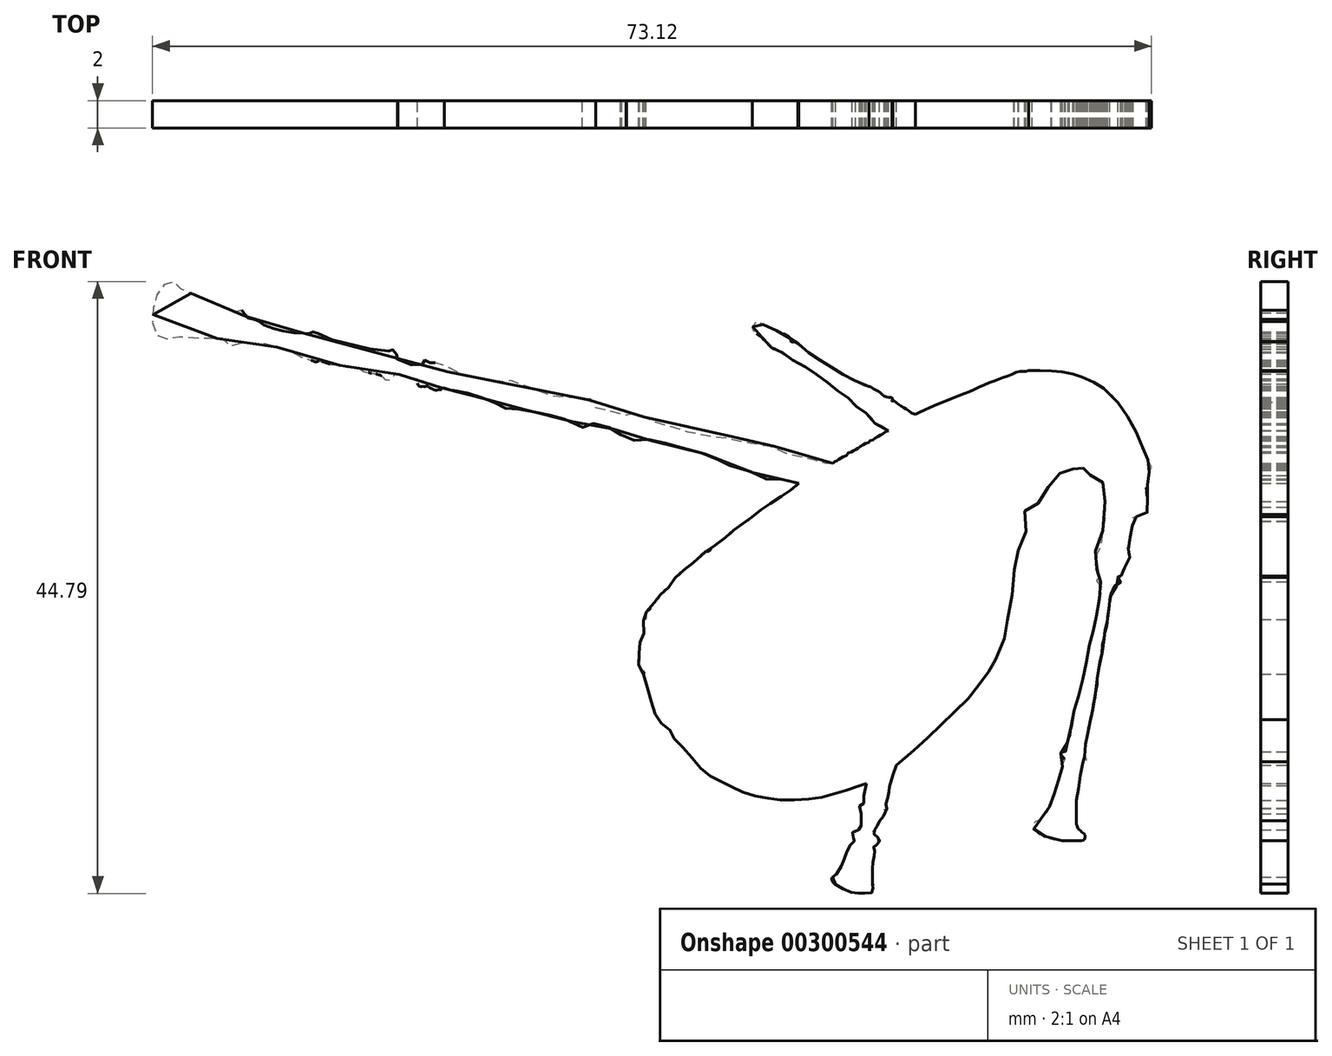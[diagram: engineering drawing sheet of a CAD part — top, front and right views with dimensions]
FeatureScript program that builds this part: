
annotation { "Feature Type Name" : "Feature", "Feature Type Description" : "" }
export const myFeature = defineFeature(function(context is Context, id is Id, definition is map)
    precondition{}
    {
        {
            var Q0;
            Q0=qCreatedBy(makeId("Front.planeOp"),FACE);
            var sketch = newSketch(context, id + "F0", { "sketchPlane" : qUnion([Q0])});
            skFitSpline(sketch, "E0", {"points": [v(-4.4, -4) * mm, v(-4.03, -5.37) * mm, v(-3.62, -6.74) * mm, v(-3.21, -7.5) * mm, v(-2.5, -8.07) * mm, v(-2.19, -8.69) * mm, v(-1.47, -9.44) * mm, v(-0.58, -10.5) * mm, v(0.27, -11.32) * mm, v(1.13, -11.8) * mm, v(1.98, -12.2) * mm, v(3.14, -12.75) * mm, v(4.3, -13) * mm, v(5.4, -13.2) * mm, v(6.8, -13.2) * mm, v(8.2, -13.1) * mm, v(9.33, -12.82) * mm, v(10.45, -12.5) * mm, v(11.54, -12.12) * mm, v(11.9, -12) * mm], "startDerivative": vector(6.1, -22.37) * mm, "endDerivative": vector(9.97, 3.21) * mm});
            skFitSpline(sketch, "E1", {"points": [v(11.9, -12) * mm, v(11.73, -12.78) * mm, v(11.66, -13.2) * mm, v(11.63, -13.38) * mm, v(11.78, -13.52) * mm, v(11.43, -13.58) * mm, v(11.44, -13.79) * mm, v(11.52, -13.94) * mm, v(11.5, -14.57) * mm, v(11.52, -15.1) * mm, v(11.5, -15.34) * mm, v(11.38, -15.4) * mm, v(11.26, -15.39) * mm, v(10.97, -15.48) * mm, v(10.88, -15.6) * mm, v(10.85, -15.8) * mm, v(10.88, -15.93) * mm, v(10.97, -15.98) * mm, v(11.04, -16.07) * mm, v(11.1, -16.14) * mm, v(11.03, -16.21) * mm, v(10.88, -16.25) * mm, v(10.77, -16.42) * mm, v(10.69, -16.6) * mm, v(10.56, -16.86) * mm, v(10.45, -17.04) * mm, v(10.34, -17.33) * mm, v(10.24, -17.6) * mm, v(10.13, -17.9) * mm, v(10, -18.16) * mm, v(9.82, -18.53) * mm, v(9.64, -18.75) * mm, v(9.65, -18.85) * mm, v(9.4, -18.86) * mm, v(9.46, -19.23) * mm, v(9.72, -19.44) * mm, v(10.06, -19.64) * mm, v(10.31, -19.75) * mm, v(10.67, -19.93) * mm, v(11, -20.02) * mm, v(11.16, -20.02) * mm, v(11.35, -20.03) * mm, v(11.6, -20.04) * mm, v(11.8, -20.04) * mm, v(12.04, -20.05) * mm, v(12.25, -20) * mm, v(12.4, -19.91) * mm, v(12.44, -19.78) * mm, v(12.37, -19.69) * mm, v(12.37, -19.65) * mm, v(12.38, -19.5) * mm, v(12.36, -19.37) * mm, v(12.34, -19.35) * mm], "startDerivative": vector(-5.6, -22.68) * mm, "endDerivative": vector(-3.27, 1.97) * mm});
            skFitSpline(sketch, "E2", {"points": [v(12.34, -19.35) * mm, v(12.34, -19.23) * mm, v(12.35, -19.04) * mm, v(12.34, -18.88) * mm, v(12.34, -18.73) * mm, v(12.34, -18.54) * mm, v(12.34, -18.4) * mm, v(12.34, -18.26) * mm, v(12.34, -18.1) * mm, v(12.34, -17.94) * mm, v(12.4, -17.62) * mm, v(12.44, -17.4) * mm, v(12.52, -17.17) * mm, v(12.52, -17.09) * mm, v(12.52, -16.96) * mm, v(12.5, -16.84) * mm, v(12.44, -16.8) * mm, v(12.44, -16.68) * mm, v(12.4, -16.56) * mm, v(12.53, -16.51) * mm, v(12.65, -16.5) * mm, v(12.76, -16.43) * mm, v(12.81, -16.33) * mm, v(12.85, -16.2) * mm, v(12.84, -16.08) * mm, v(12.76, -15.97) * mm, v(12.65, -15.9) * mm, v(12.5, -15.77) * mm, v(12.44, -15.67) * mm, v(12.44, -15.53) * mm, v(12.49, -15.42) * mm, v(12.54, -15.32) * mm, v(12.61, -15.2) * mm, v(12.7, -15.1) * mm, v(12.75, -15.03) * mm, v(12.83, -14.81) * mm, v(12.93, -14.64) * mm, v(13.1, -14.46) * mm, v(13.2, -14.33) * mm, v(13.3, -14.21) * mm, v(13.26, -13.95) * mm, v(13.23, -13.8) * mm, v(13.41, -13.83) * mm, v(13.3, -13.63) * mm, v(13.3, -13.52) * mm, v(13.37, -13.32) * mm, v(13.44, -13.13) * mm, v(13.5, -12.8) * mm, v(13.54, -12.65) * mm, v(13.57, -12.48) * mm, v(13.58, -12.34) * mm, v(13.6, -12.15) * mm, v(13.92, -11.21) * mm, v(14.09, -10.66) * mm], "startDerivative": vector(-0.15, 7.17) * mm, "endDerivative": vector(4.14, 13.76) * mm});
            skFitSpline(sketch, "E3", {"points": [v(14.09, -10.66) * mm, v(14.34, -10.47) * mm, v(14.73, -10.14) * mm, v(15.12, -9.8) * mm, v(15.34, -9.6) * mm, v(15.6, -9.39) * mm, v(15.81, -9.2) * mm, v(16.03, -9) * mm, v(16.28, -8.77) * mm, v(16.46, -8.6) * mm, v(16.66, -8.46) * mm, v(16.9, -8.22) * mm, v(17.09, -8.01) * mm, v(17.3, -7.82) * mm, v(17.47, -7.6) * mm, v(17.74, -7.44) * mm, v(17.93, -7.24) * mm, v(18.1, -7.05) * mm, v(18.3, -6.8) * mm, v(18.52, -6.66) * mm, v(18.7, -6.43) * mm, v(19, -6.18) * mm, v(19.2, -5.92) * mm, v(19.35, -5.77) * mm, v(19.6, -5.58) * mm, v(19.69, -5.43) * mm, v(19.85, -5.23) * mm, v(20.02, -4.98) * mm, v(20.12, -4.8) * mm, v(20.27, -4.56) * mm, v(20.43, -4.44) * mm, v(20.54, -4.24) * mm, v(20.63, -4.08) * mm, v(20.8, -3.88) * mm, v(20.88, -3.71) * mm, v(20.95, -3.58) * mm, v(21.02, -3.48) * mm, v(21.15, -3.33) * mm, v(21.22, -3.17) * mm, v(21.29, -3.06) * mm, v(21.36, -2.93) * mm, v(21.42, -2.78) * mm, v(21.73, -2.09) * mm, v(21.9, -1.7) * mm, v(21.98, -1.45) * mm, v(22.06, -1.14) * mm, v(22.12, -0.89) * mm, v(22.15, -0.65) * mm, v(22.19, -0.35) * mm, v(22.2, -0.12) * mm, v(22.28, 0.29) * mm, v(22.33, 0.67) * mm, v(22.53, 1.49) * mm, v(22.58, 1.94) * mm, v(22.69, 2.7) * mm, v(22.69, 3.04) * mm, v(22.73, 3.47) * mm, v(22.7, 3.96) * mm, v(22.71, 4.37) * mm, v(22.87, 4.56) * mm, v(23.03, 4.74) * mm, v(23, 5.17) * mm, v(23.15, 5.44) * mm, v(23.33, 5.75) * mm, v(23.51, 6.09) * mm, v(23.58, 6.46) * mm, v(23.6, 6.85) * mm, v(23.58, 7.1) * mm, v(23.55, 7.45) * mm, v(23.52, 7.66) * mm, v(23.54, 8.1) * mm, v(23.72, 8.18) * mm, v(23.96, 8.22) * mm, v(24.14, 8.23) * mm, v(24.36, 8.4) * mm, v(24.5, 8.55) * mm, v(24.63, 8.78) * mm, v(24.73, 8.9) * mm, v(24.86, 9.16) * mm, v(25.04, 9.45) * mm, v(25.28, 9.78) * mm, v(25.54, 10.22) * mm, v(25.73, 10.4) * mm, v(25.86, 10.5) * mm, v(25.98, 10.66) * mm, v(26.05, 10.71) * mm, v(26.16, 10.88) * mm, v(26.3, 11) * mm, v(26.54, 10.96) * mm, v(26.66, 10.92) * mm, v(26.88, 10.96) * mm, v(27.05, 11.03) * mm, v(27.22, 11.14) * mm, v(27.34, 11.28) * mm, v(27.46, 11.34) * mm, v(27.6, 11.25) * mm, v(27.68, 11.17) * mm, v(27.71, 11.1) * mm, v(27.84, 11.07) * mm, v(27.99, 11.06) * mm, v(28.16, 11.06) * mm, v(28.27, 11.04) * mm, v(28.28, 10.9) * mm, v(28.27, 10.77) * mm, v(28.26, 10.65) * mm, v(28.3, 10.54) * mm, v(28.4, 10.42) * mm, v(28.55, 10.33) * mm, v(28.74, 10.22) * mm, v(28.88, 10.23) * mm, v(29.13, 10.16) * mm, v(29.2, 9.9) * mm, v(29.11, 9.54) * mm, v(29.1, 9.24) * mm, v(29.23, 8.92) * mm, v(29.37, 8.63) * mm], "startDerivative": vector(24.42, 19.4) * mm, "endDerivative": vector(13.5, -29.6) * mm});
            skFitSpline(sketch, "E4", {"points": [v(29.37, 8.63) * mm, v(29.37, 8.2) * mm, v(29.37, 7.91) * mm, v(29.37, 7.56) * mm, v(29.26, 7.1) * mm, v(29.22, 6.78) * mm, v(29.18, 6.27) * mm, v(29.08, 5.97) * mm, v(29.05, 5.62) * mm, v(29.05, 5.36) * mm, v(28.95, 5.28) * mm, v(28.82, 5.2) * mm, v(28.67, 5.1) * mm, v(28.69, 4.9) * mm, v(28.77, 4.7) * mm, v(28.82, 4.64) * mm, v(28.73, 4.48) * mm, v(28.67, 4.37) * mm, v(28.77, 4.31) * mm, v(28.78, 4.1) * mm, v(28.74, 3.85) * mm, v(28.75, 3.65) * mm, v(28.77, 3.47) * mm, v(28.93, 3.33) * mm, v(28.73, 3.29) * mm, v(28.65, 3.13) * mm, v(28.69, 2.94) * mm, v(28.77, 2.82) * mm, v(28.93, 2.77) * mm, v(29.07, 2.76) * mm, v(29.12, 2.63) * mm, v(29.12, 2.51) * mm, v(29.1, 2.3) * mm, v(29.08, 2.14) * mm, v(29.08, 1.97) * mm, v(29.02, 1.75) * mm, v(29.02, 1.68) * mm, v(29, 1.6) * mm, v(28.96, 1.48) * mm, v(28.91, 1.37) * mm, v(28.92, 1.19) * mm, v(28.9, 1.1) * mm, v(28.86, 0.96) * mm, v(28.83, 0.73) * mm, v(28.8, 0.6) * mm, v(28.78, 0.48) * mm, v(28.76, 0.34) * mm, v(28.73, 0.22) * mm, v(28.71, 0.11) * mm, v(28.69, 0) * mm, v(28.67, -0.08) * mm, v(28.66, -0.16) * mm, v(28.66, -0.26) * mm, v(28.62, -0.42) * mm, v(28.62, -0.48) * mm, v(28.58, -0.56) * mm, v(28.56, -0.64) * mm, v(28.53, -0.75) * mm, v(28.52, -0.82) * mm, v(28.5, -0.9) * mm, v(28.5, -0.95) * mm, v(28.46, -1.03) * mm, v(28.42, -1.15) * mm, v(28.42, -1.2) * mm, v(28.37, -1.3) * mm, v(28.35, -1.41) * mm, v(28.33, -1.53) * mm, v(28.32, -1.59) * mm, v(28.3, -1.67) * mm, v(28.24, -1.82) * mm, v(28.2, -2.09) * mm, v(28.16, -2.31) * mm, v(28.13, -2.5) * mm, v(28.1, -2.64) * mm, v(28.05, -2.82) * mm, v(28.04, -2.87) * mm, v(28.02, -2.93) * mm, v(28.02, -3) * mm, v(28.01, -3.06) * mm, v(28, -3.14) * mm, v(27.99, -3.21) * mm, v(27.97, -3.33) * mm, v(27.96, -3.4) * mm, v(27.95, -3.45) * mm, v(27.92, -3.55) * mm, v(27.88, -3.64) * mm, v(27.86, -3.85) * mm, v(27.8, -4.05) * mm, v(27.78, -4.24) * mm, v(27.73, -4.38) * mm, v(27.67, -4.54) * mm, v(27.6, -4.72) * mm, v(27.55, -4.93) * mm, v(27.5, -5.08) * mm, v(27.5, -5.2) * mm, v(27.48, -5.3) * mm, v(27.47, -5.43) * mm, v(27.44, -5.53) * mm, v(27.42, -5.65) * mm, v(27.39, -5.75) * mm, v(27.37, -5.83) * mm, v(27.34, -5.94) * mm, v(27.32, -6.03) * mm, v(27.3, -6.13) * mm, v(27.29, -6.2) * mm, v(27.25, -6.26) * mm, v(27.24, -6.34) * mm, v(27.2, -6.43) * mm, v(27.16, -6.54) * mm, v(27.11, -6.63) * mm, v(27.1, -6.78) * mm, v(27.05, -7) * mm, v(27, -7.19) * mm, v(27, -7.33) * mm, v(26.95, -7.56) * mm, v(26.94, -7.64) * mm, v(26.9, -7.75) * mm, v(26.87, -7.9) * mm, v(26.84, -8.02) * mm, v(26.82, -8.16) * mm, v(26.8, -8.35) * mm, v(26.78, -8.47) * mm, v(26.77, -8.57) * mm, v(26.76, -8.63) * mm, v(26.7, -8.67) * mm, v(26.68, -8.78) * mm, v(26.67, -8.86) * mm, v(26.64, -8.93) * mm, v(26.62, -9.04) * mm, v(26.6, -9.13) * mm, v(26.57, -9.22) * mm, v(26.56, -9.3) * mm, v(26.53, -9.4) * mm, v(26.52, -9.48) * mm, v(26.48, -9.6) * mm, v(26.47, -9.67) * mm, v(26.33, -9.68) * mm, v(26.26, -9.68) * mm, v(26.23, -9.7) * mm, v(26.16, -9.76) * mm, v(26.13, -9.87) * mm, v(26.16, -9.9) * mm, v(26.2, -9.97) * mm, v(26.27, -10.03) * mm, v(26.29, -10.06) * mm, v(26.35, -10.12) * mm, v(26.4, -10.18) * mm, v(26.36, -10.37) * mm, v(26.33, -10.49) * mm, v(26.27, -10.6) * mm, v(26.25, -10.66) * mm, v(26.25, -10.76) * mm, v(26.21, -10.82) * mm, v(26.2, -10.95) * mm, v(26.16, -11.06) * mm, v(26.14, -11.16) * mm, v(26.12, -11.21) * mm, v(26.12, -11.28) * mm, v(26.1, -11.35) * mm, v(26.05, -11.48) * mm, v(26.04, -11.56) * mm, v(26, -11.65) * mm, v(25.97, -11.73) * mm, v(25.91, -11.83) * mm, v(25.9, -11.94) * mm, v(25.88, -12) * mm, v(25.86, -12.15) * mm, v(25.83, -12.15) * mm, v(25.8, -12.24) * mm, v(25.76, -12.34) * mm, v(25.75, -12.48) * mm, v(25.74, -12.56) * mm, v(25.68, -12.65) * mm, v(25.65, -12.73) * mm, v(25.63, -12.8) * mm, v(25.6, -12.95) * mm, v(25.59, -13) * mm, v(25.53, -13.07) * mm, v(25.5, -13.1) * mm, v(25.47, -13.18) * mm, v(25.44, -13.28) * mm, v(25.45, -13.36) * mm, v(25.4, -13.44) * mm, v(25.38, -13.48) * mm, v(25.34, -13.62) * mm, v(25.31, -13.7) * mm, v(25.26, -13.84) * mm, v(25.18, -14) * mm, v(25.13, -14.12) * mm, v(25.07, -14.21) * mm, v(25.03, -14.21) * mm, v(24.97, -14.32) * mm, v(24.9, -14.38) * mm, v(24.85, -14.43) * mm, v(24.8, -14.48) * mm, v(24.74, -14.52) * mm, v(24.6, -14.65) * mm, v(24.55, -14.7) * mm, v(24.4, -14.76) * mm, v(24.34, -14.77) * mm, v(24.27, -14.79) * mm, v(24.1, -14.8) * mm, v(24.07, -14.9) * mm, v(24.04, -15.05) * mm, v(24.08, -15.18) * mm, v(24.11, -15.3) * mm, v(24.16, -15.35) * mm, v(24.2, -15.42) * mm, v(24.27, -15.47) * mm, v(24.33, -15.51) * mm, v(24.42, -15.58) * mm, v(24.45, -15.61) * mm, v(24.5, -15.66) * mm, v(24.6, -15.7) * mm, v(24.63, -15.75) * mm, v(24.7, -15.78) * mm, v(24.78, -15.83) * mm, v(24.93, -15.86) * mm, v(25, -15.88) * mm, v(25.1, -15.94) * mm, v(25.21, -16) * mm, v(25.33, -16.02) * mm, v(25.46, -16.07) * mm, v(25.58, -16.1) * mm, v(25.67, -16.13) * mm, v(25.73, -16.13) * mm, v(25.92, -16.14) * mm, v(26.2, -16.19) * mm], "startDerivative": vector(0.28, -53.15) * mm, "endDerivative": vector(42.65, -6.9) * mm});
            skFitSpline(sketch, "E5", {"points": [v(26.2, -16.19) * mm, v(26.4, -16.19) * mm, v(26.56, -16.19) * mm, v(26.83, -16.19) * mm, v(26.97, -16.19) * mm, v(27.24, -16.19) * mm, v(27.3, -16.19) * mm, v(27.54, -16.19) * mm, v(27.7, -16.19) * mm, v(27.84, -16.1) * mm, v(27.9, -16.02) * mm, v(27.9, -15.87) * mm, v(27.88, -15.76) * mm, v(27.84, -15.7) * mm, v(27.8, -15.65) * mm, v(27.72, -15.6) * mm, v(27.66, -15.54) * mm, v(27.6, -15.48) * mm, v(27.55, -15.43) * mm, v(27.5, -15.4) * mm, v(27.46, -15.37) * mm, v(27.4, -15.3) * mm, v(27.37, -15.3) * mm, v(27.34, -15.18) * mm, v(27.3, -15.03) * mm, v(27.27, -14.93) * mm, v(27.27, -14.8) * mm, v(27.28, -14.71) * mm], "startDerivative": vector(4.3, 0) * mm, "endDerivative": vector(0.55, 2.5) * mm});
            skFitSpline(sketch, "E6", {"points": [v(27.28, -14.71) * mm, v(27.27, -14.63) * mm, v(27.27, -14.56) * mm, v(27.27, -14.5) * mm, v(27.27, -14.43) * mm, v(27.27, -14.36) * mm, v(27.27, -14.3) * mm, v(27.27, -14.23) * mm, v(27.27, -14.17) * mm, v(27.28, -14.13) * mm, v(27.28, -14.04) * mm, v(27.28, -13.99) * mm, v(27.28, -13.92) * mm, v(27.28, -13.9) * mm, v(27.28, -13.83) * mm, v(27.28, -13.77) * mm, v(27.28, -13.7) * mm, v(27.3, -13.66) * mm, v(27.3, -13.62) * mm, v(27.3, -13.58) * mm, v(27.3, -13.56) * mm, v(27.3, -13.48) * mm, v(27.3, -13.46) * mm, v(27.28, -13.35) * mm, v(27.28, -13.24) * mm, v(27.28, -13.14) * mm, v(27.28, -13.06) * mm, v(27.28, -13) * mm, v(27.4, -12.93) * mm, v(27.4, -12.83) * mm, v(27.4, -12.63) * mm, v(27.4, -12.57) * mm, v(27.4, -12.5) * mm, v(27.4, -12.43) * mm, v(27.46, -12.35) * mm, v(27.46, -12.22) * mm, v(27.46, -12.15) * mm, v(27.47, -12.04) * mm, v(27.47, -11.94) * mm, v(27.47, -11.8) * mm, v(27.47, -11.65) * mm, v(27.54, -11.56) * mm, v(27.54, -11.48) * mm, v(27.54, -11.38) * mm, v(27.54, -11.3) * mm, v(27.54, -11.18) * mm, v(27.54, -11.09) * mm, v(27.7, -10.95) * mm, v(27.7, -10.7) * mm, v(27.7, -10.62) * mm, v(27.7, -10.54) * mm, v(27.75, -10.5) * mm, v(27.8, -10.42) * mm, v(27.84, -10.42) * mm, v(27.91, -10.4) * mm, v(27.93, -10.4) * mm, v(27.96, -10.37) * mm, v(27.98, -10.34) * mm, v(28.01, -10.31) * mm, v(28.02, -10.27) * mm, v(28.02, -10.24) * mm, v(28.02, -10.18) * mm, v(28, -10.14) * mm, v(27.98, -10.1) * mm, v(27.9, -10.05) * mm, v(27.85, -10) * mm, v(27.87, -9.96) * mm, v(27.87, -9.85) * mm, v(27.86, -9.81) * mm, v(27.87, -9.67) * mm, v(27.86, -9.56) * mm, v(27.88, -9.48) * mm, v(27.93, -9.35) * mm, v(27.93, -9.23) * mm, v(27.94, -9.17) * mm, v(27.95, -9.12) * mm, v(27.97, -9.01) * mm, v(28, -8.94) * mm, v(28.03, -8.8) * mm, v(28.03, -8.78) * mm, v(28.05, -8.67) * mm, v(28.04, -8.63) * mm, v(28.05, -8.59) * mm, v(28.07, -8.52) * mm, v(28.08, -8.45) * mm, v(28.09, -8.42) * mm, v(28.1, -8.35) * mm, v(28.1, -8.32) * mm, v(28.1, -8.28) * mm, v(28.1, -8.2) * mm, v(28.1, -8.16) * mm, v(28.12, -8.1) * mm, v(28.14, -8.06) * mm, v(28.15, -8) * mm, v(28.15, -7.95) * mm, v(28.16, -7.93) * mm, v(28.18, -7.88) * mm, v(28.2, -7.83) * mm, v(28.22, -7.77) * mm, v(28.23, -7.73) * mm, v(28.24, -7.7) * mm, v(28.25, -7.65) * mm, v(28.26, -7.59) * mm, v(28.26, -7.54) * mm, v(28.27, -7.47) * mm, v(28.27, -7.46) * mm, v(28.27, -7.45) * mm, v(28.3, -7.37) * mm, v(28.3, -7.37) * mm, v(28.3, -7.33) * mm, v(28.3, -7.33) * mm, v(28.31, -7.28) * mm, v(28.32, -7.21) * mm, v(28.34, -7.18) * mm, v(28.36, -7.13) * mm, v(28.37, -7.1) * mm, v(28.37, -7.08) * mm, v(28.38, -7.05) * mm, v(28.38, -7.04) * mm, v(28.38, -7) * mm, v(28.39, -6.95) * mm, v(28.39, -6.92) * mm, v(28.39, -6.9) * mm, v(28.4, -6.87) * mm, v(28.42, -6.81) * mm, v(28.43, -6.78) * mm, v(28.43, -6.74) * mm, v(28.44, -6.7) * mm, v(28.44, -6.67) * mm, v(28.45, -6.65) * mm, v(28.45, -6.63) * mm, v(28.47, -6.58) * mm, v(28.47, -6.56) * mm, v(28.48, -6.52) * mm, v(28.48, -6.5) * mm, v(28.49, -6.47) * mm, v(28.49, -6.45) * mm, v(28.49, -6.41) * mm, v(28.5, -6.38) * mm, v(28.49, -6.36) * mm, v(28.5, -6.34) * mm, v(28.5, -6.32) * mm, v(28.5, -6.3) * mm, v(28.5, -6.28) * mm, v(28.51, -6.21) * mm, v(28.53, -6.1) * mm, v(28.57, -6) * mm, v(28.61, -5.9) * mm, v(28.64, -5.76) * mm, v(28.63, -5.64) * mm, v(28.62, -5.57) * mm, v(28.62, -5.52) * mm, v(28.65, -5.43) * mm, v(28.66, -5.35) * mm, v(28.67, -5.3) * mm, v(28.68, -5.23) * mm, v(28.7, -5.17) * mm, v(28.72, -5.09) * mm, v(28.73, -5.02) * mm, v(28.76, -4.95) * mm, v(28.77, -4.86) * mm, v(28.79, -4.75) * mm, v(28.79, -4.74) * mm, v(28.8, -4.7) * mm, v(28.8, -4.62) * mm, v(28.8, -4.53) * mm, v(28.79, -4.5) * mm, v(28.79, -4.42) * mm, v(28.79, -4.34) * mm, v(28.8, -4.28) * mm, v(28.8, -4.25) * mm, v(28.8, -4.19) * mm, v(28.8, -4.15) * mm, v(28.84, -3.96) * mm, v(28.84, -3.81) * mm, v(28.9, -3.61) * mm, v(28.91, -3.54) * mm, v(28.95, -3.42) * mm, v(28.96, -3.29) * mm, v(28.96, -3.17) * mm, v(29, -3.03) * mm, v(29.06, -2.89) * mm, v(29.12, -2.76) * mm, v(29.15, -2.62) * mm, v(29.15, -2.5) * mm, v(29.17, -2.37) * mm, v(29.17, -2.27) * mm, v(29.18, -2.1) * mm, v(29.2, -2) * mm, v(29.18, -1.83) * mm, v(29.18, -1.8) * mm, v(29.26, -1.63) * mm, v(29.26, -1.59) * mm, v(29.26, -1.52) * mm, v(29.28, -1.47) * mm, v(29.29, -1.44) * mm, v(29.3, -1.4) * mm, v(29.3, -1.36) * mm, v(29.32, -1.3) * mm, v(29.32, -1.24) * mm, v(29.33, -1.2) * mm, v(29.33, -1.15) * mm, v(29.33, -1.13) * mm, v(29.33, -1.12) * mm, v(29.33, -1.05) * mm, v(29.32, -0.98) * mm, v(29.34, -0.9) * mm, v(29.37, -0.87) * mm, v(29.37, -0.85) * mm, v(29.37, -0.8) * mm, v(29.41, -0.73) * mm, v(29.43, -0.68) * mm, v(29.45, -0.58) * mm, v(29.44, -0.52) * mm, v(29.46, -0.46) * mm, v(29.46, -0.45) * mm, v(29.46, -0.42) * mm, v(29.47, -0.38) * mm, v(29.49, -0.34) * mm, v(29.5, -0.3) * mm, v(29.53, -0.26) * mm, v(29.53, -0.2) * mm, v(29.53, -0.18) * mm, v(29.54, -0.13) * mm, v(29.56, -0.09) * mm, v(29.56, -0.03) * mm, v(29.56, 0) * mm, v(29.56, 0.11) * mm, v(29.54, 0.2) * mm, v(29.53, 0.28) * mm, v(29.56, 0.46) * mm, v(29.6, 0.6) * mm, v(29.63, 0.72) * mm, v(29.67, 0.9) * mm, v(29.67, 0.94) * mm, v(29.68, 1.01) * mm, v(29.7, 1.1) * mm, v(29.7, 1.2) * mm, v(29.7, 1.3) * mm, v(29.7, 1.42) * mm, v(29.71, 1.53) * mm, v(29.73, 1.61) * mm, v(29.76, 1.68) * mm, v(29.78, 1.8) * mm, v(29.82, 1.9) * mm, v(29.85, 1.97) * mm, v(29.88, 2.09) * mm, v(29.92, 2.22) * mm, v(29.97, 2.33) * mm, v(30.08, 2.46) * mm, v(30.17, 2.48) * mm, v(30.29, 2.5) * mm, v(30.33, 2.5) * mm, v(30.43, 2.6) * mm, v(30.49, 2.7) * mm, v(30.5, 2.77) * mm, v(30.5, 2.82) * mm, v(30.5, 2.9) * mm, v(30.48, 2.93) * mm, v(30.47, 2.96) * mm, v(30.4, 3.02) * mm, v(30.33, 3.08) * mm, v(30.33, 3.08) * mm], "startDerivative": vector(-1.8, 19.18) * mm, "endDerivative": vector(-3.69, -1.3) * mm});
            skFitSpline(sketch, "E7", {"points": [v(30.33, 3.08) * mm, v(30.33, 3.14) * mm, v(30.4, 3.15) * mm, v(30.46, 3.17) * mm, v(30.52, 3.18) * mm, v(30.52, 3.18) * mm], "startDerivative": vector(-0.05, 0.33) * mm, "endDerivative": vector(0.07, 0) * mm});
            skFitSpline(sketch, "E8", {"points": [v(30.52, 3.18) * mm, v(30.58, 3.18) * mm, v(30.61, 3.2) * mm, v(30.65, 3.23) * mm, v(30.66, 3.3) * mm, v(30.66, 3.35) * mm, v(30.65, 3.4) * mm, v(30.66, 3.5) * mm, v(30.67, 3.55) * mm, v(30.7, 3.61) * mm, v(30.74, 3.69) * mm, v(30.8, 3.77) * mm, v(30.82, 3.84) * mm, v(30.87, 3.93) * mm, v(30.9, 4.03) * mm, v(30.95, 4.1) * mm, v(30.94, 4.22) * mm, v(30.94, 4.3) * mm, v(31.05, 4.38) * mm, v(31.1, 4.42) * mm, v(31.15, 4.48) * mm, v(31.2, 4.58) * mm, v(31.2, 4.73) * mm, v(31.15, 4.81) * mm, v(31.09, 4.88) * mm, v(30.98, 4.93) * mm, v(30.95, 4.94) * mm, v(30.86, 5) * mm, v(30.83, 5.03) * mm, v(31.05, 5.1) * mm, v(31.08, 5.21) * mm, v(31.09, 5.32) * mm, v(31.1, 5.39) * mm, v(31.1, 5.5) * mm, v(31.1, 5.56) * mm, v(31.1, 5.64) * mm, v(31.12, 5.73) * mm, v(31.14, 5.84) * mm, v(31.16, 5.94) * mm, v(31.2, 6.03) * mm, v(31.22, 6.12) * mm, v(31.24, 6.18) * mm, v(31.26, 6.24) * mm, v(31.28, 6.32) * mm, v(31.29, 6.44) * mm, v(31.29, 6.51) * mm, v(31.29, 6.57) * mm, v(31.32, 6.67) * mm, v(31.34, 6.78) * mm, v(31.37, 6.88) * mm, v(31.37, 7.04) * mm, v(31.38, 7.13) * mm, v(31.38, 7.2) * mm, v(31.41, 7.29) * mm, v(31.43, 7.38) * mm, v(31.43, 7.46) * mm, v(31.45, 7.53) * mm, v(31.53, 7.54) * mm, v(31.65, 7.54) * mm, v(31.8, 7.58) * mm, v(31.88, 7.65) * mm, v(31.93, 7.68) * mm, v(32, 7.68) * mm, v(32.14, 7.62) * mm, v(32.26, 7.67) * mm, v(32.28, 7.7) * mm, v(32.38, 7.76) * mm, v(32.42, 7.8) * mm, v(32.47, 7.86) * mm, v(32.5, 8.12) * mm, v(32.49, 8.26) * mm, v(32.48, 8.37) * mm, v(32.48, 8.48) * mm, v(32.5, 8.57) * mm, v(32.5, 8.68) * mm, v(32.5, 8.75) * mm, v(32.46, 8.97) * mm, v(32.44, 9.04) * mm, v(32.41, 9.15) * mm, v(32.41, 9.35) * mm, v(32.4, 9.53) * mm, v(32.38, 9.64) * mm, v(32.4, 9.77) * mm, v(32.44, 9.82) * mm, v(32.47, 9.87) * mm, v(32.51, 9.92) * mm, v(32.58, 10) * mm, v(32.59, 10.23) * mm, v(32.58, 10.31) * mm, v(32.59, 10.4) * mm, v(32.6, 10.49) * mm, v(32.6, 10.53) * mm, v(32.6, 10.54) * mm, v(32.6, 10.7) * mm, v(32.62, 10.84) * mm, v(32.68, 10.96) * mm, v(32.71, 11.02) * mm, v(32.77, 11.12) * mm, v(32.76, 11.23) * mm, v(32.7, 11.33) * mm, v(32.64, 11.44) * mm, v(32.56, 11.57) * mm, v(32.5, 11.73) * mm, v(32.44, 11.89) * mm, v(32.39, 11.98) * mm, v(32.35, 12.07) * mm, v(32.33, 12.15) * mm, v(32.29, 12.23) * mm, v(32.24, 12.3) * mm, v(32.2, 12.37) * mm, v(32.15, 12.45) * mm, v(32.12, 12.67) * mm, v(32.04, 12.86) * mm, v(31.96, 13.04) * mm, v(31.85, 13.25) * mm, v(31.8, 13.42) * mm, v(31.7, 13.6) * mm, v(31.65, 13.73) * mm, v(31.58, 13.83) * mm, v(31.49, 13.97) * mm, v(31.32, 14.08) * mm, v(31.27, 14.36) * mm, v(31.16, 14.44) * mm, v(31.05, 14.75) * mm, v(30.94, 14.97) * mm, v(30.85, 15.13) * mm, v(30.72, 15.3) * mm, v(30.66, 15.37) * mm, v(30.58, 15.51) * mm, v(30.5, 15.71) * mm, v(30.34, 15.86) * mm, v(30.25, 15.96) * mm, v(30.13, 16.08) * mm, v(30, 16.16) * mm, v(29.7, 16.67) * mm, v(29.37, 16.78) * mm, v(29.27, 16.94) * mm, v(29.18, 16.99) * mm, v(29.11, 17.07) * mm, v(29.05, 17.1) * mm, v(28.95, 17.16) * mm, v(28.91, 17.18) * mm, v(28.84, 17.22) * mm, v(28.76, 17.25) * mm, v(28.69, 17.3) * mm, v(28.63, 17.34) * mm, v(28.5, 17.39) * mm, v(28.47, 17.4) * mm, v(28.4, 17.43) * mm, v(28.3, 17.47) * mm, v(28.2, 17.52) * mm, v(28.04, 17.62) * mm, v(27.98, 17.65) * mm, v(27.8, 17.7) * mm, v(27.7, 17.73) * mm, v(27.64, 17.76) * mm, v(27.54, 17.8) * mm, v(27.5, 17.8) * mm, v(27.46, 17.82) * mm, v(27.4, 17.85) * mm, v(27.34, 17.87) * mm, v(27.28, 17.89) * mm, v(27.22, 17.92) * mm, v(27.16, 17.94) * mm, v(27.11, 17.95) * mm, v(27.06, 17.97) * mm, v(27, 17.98) * mm, v(26.97, 18) * mm, v(26.87, 18.01) * mm, v(26.83, 18.02) * mm, v(26.73, 18.03) * mm, v(26.65, 18.03) * mm, v(26.57, 18.04) * mm, v(26.54, 18.05) * mm, v(26.47, 18.07) * mm, v(26.43, 18.08) * mm, v(26.29, 18.12) * mm, v(26.23, 18.13) * mm, v(26.21, 18.14) * mm, v(26.15, 18.15) * mm, v(26.03, 18.16) * mm, v(25.93, 18.16) * mm, v(25.87, 18.17) * mm, v(25.75, 18.18) * mm, v(25.7, 18.18) * mm, v(25.63, 18.18) * mm, v(25.58, 18.18) * mm, v(25.52, 18.18) * mm, v(25.45, 18.19) * mm, v(25.35, 18.2) * mm, v(25.22, 18.2) * mm, v(25.11, 18.2) * mm, v(25.03, 18.2) * mm, v(24.95, 18.2) * mm, v(24.87, 18.22) * mm, v(24.8, 18.22) * mm, v(24.71, 18.22) * mm, v(24.64, 18.22) * mm, v(24.59, 18.22) * mm, v(24.52, 18.22) * mm, v(24.45, 18.23) * mm, v(24.39, 18.23) * mm, v(24.32, 18.23) * mm, v(24.24, 18.23) * mm, v(24.14, 18.23) * mm, v(24.05, 18.23) * mm, v(23.99, 18.23) * mm, v(23.9, 18.21) * mm, v(23.79, 18.21) * mm], "startDerivative": vector(16.41, -1.75) * mm, "endDerivative": vector(-23.2, 1) * mm});
            skFitSpline(sketch, "E9", {"points": [v(23.79, 18.21) * mm, v(23.44, 18.17) * mm, v(23.12, 18.17) * mm, v(22.4, 17.9) * mm, v(21.68, 17.62) * mm, v(20.76, 17.3) * mm, v(19.67, 16.78) * mm, v(18.58, 16.34) * mm, v(16.51, 15.51) * mm, v(15.48, 15.02) * mm], "startDerivative": vector(-5.31, -0.96) * mm, "endDerivative": vector(-7.3, -3.62) * mm});
            skFitSpline(sketch, "E10", {"points": [v(15.48, 15.02) * mm, v(15.13, 15.17) * mm, v(14.9, 15.36) * mm, v(14.72, 15.45) * mm, v(14.46, 15.62) * mm, v(14.27, 15.74) * mm, v(14.08, 15.88) * mm, v(13.92, 16) * mm, v(13.77, 15.99) * mm, v(13.83, 16.14) * mm, v(13.79, 16.24) * mm, v(13.66, 16.25) * mm, v(13.5, 16.25) * mm, v(13.38, 16.29) * mm, v(13.14, 16.4) * mm, v(13.02, 16.5) * mm, v(12.91, 16.61) * mm, v(12.8, 16.69) * mm, v(12.7, 16.74) * mm, v(12.63, 16.8) * mm, v(12.54, 16.84) * mm, v(12.4, 16.88) * mm, v(12.3, 16.95) * mm, v(12.22, 17.03) * mm, v(12.18, 17.05) * mm, v(12.1, 17.07) * mm, v(12.08, 17.07) * mm], "startDerivative": vector(-6.1, 2.06) * mm, "endDerivative": vector(-1.46, -0.08) * mm});
            skFitSpline(sketch, "E11", {"points": [v(12.08, 17.07) * mm, v(11.9, 17.07) * mm, v(11.79, 17.07) * mm, v(11.6, 17.17) * mm, v(11.44, 17.26) * mm, v(11.32, 17.29) * mm, v(11.22, 17.35) * mm, v(11.07, 17.45) * mm, v(11.03, 17.5) * mm, v(10.88, 17.57) * mm, v(10.83, 17.6) * mm, v(10.74, 17.66) * mm, v(10.63, 17.7) * mm, v(10.54, 17.76) * mm, v(10.48, 17.81) * mm, v(10.36, 17.87) * mm, v(10.27, 17.89) * mm, v(10.15, 17.94) * mm, v(10.04, 17.99) * mm, v(9.97, 18.03) * mm, v(9.84, 18.08) * mm, v(9.74, 18.17) * mm, v(9.65, 18.23) * mm, v(9.54, 18.3) * mm, v(9.47, 18.37) * mm, v(9.38, 18.44) * mm, v(9.3, 18.5) * mm, v(9.18, 18.56) * mm, v(9.1, 18.6) * mm, v(9, 18.63) * mm, v(8.91, 18.67) * mm, v(8.76, 18.76) * mm, v(8.68, 18.83) * mm, v(8.62, 18.9) * mm, v(8.57, 18.94) * mm, v(8.45, 19.01) * mm, v(8.35, 19.07) * mm, v(8.26, 19.11) * mm, v(8.2, 19.15) * mm, v(8.07, 19.24) * mm, v(7.98, 19.3) * mm, v(7.9, 19.36) * mm, v(7.8, 19.47) * mm, v(7.71, 19.51) * mm, v(7.65, 19.54) * mm, v(7.56, 19.6) * mm, v(7.48, 19.68) * mm, v(7.35, 19.78) * mm, v(7.23, 19.9) * mm, v(7.1, 19.97) * mm, v(7, 20.05) * mm, v(6.9, 20.1) * mm, v(6.93, 20.2) * mm, v(6.93, 20.25) * mm, v(6.93, 20.3) * mm, v(6.8, 20.33) * mm, v(6.66, 20.34) * mm, v(6.55, 20.33) * mm, v(6.47, 20.33) * mm, v(6.4, 20.33) * mm, v(6.38, 20.39) * mm, v(6.36, 20.51) * mm, v(6.3, 20.61) * mm, v(6.23, 20.7) * mm, v(6.17, 20.76) * mm, v(6.1, 20.8) * mm, v(6.02, 20.83) * mm, v(5.87, 20.9) * mm, v(5.81, 20.93) * mm, v(5.52, 21.08) * mm, v(5.32, 21.15) * mm, v(5.2, 21.2) * mm, v(5.07, 21.28) * mm, v(4.88, 21.33) * mm, v(4.8, 21.35) * mm, v(4.7, 21.4) * mm, v(4.6, 21.46) * mm, v(4.49, 21.52) * mm, v(4.35, 21.6) * mm, v(4.2, 21.67) * mm, v(4.06, 21.74) * mm, v(3.99, 21.78) * mm, v(3.88, 21.83) * mm, v(3.79, 21.71) * mm, v(3.73, 21.68) * mm, v(3.67, 21.59) * mm, v(3.61, 21.48) * mm, v(3.58, 21.4) * mm, v(3.56, 21.28) * mm, v(3.66, 21.12) * mm, v(3.8, 21.05) * mm, v(3.84, 20.97) * mm, v(3.88, 20.92) * mm, v(4.02, 20.8) * mm, v(4.14, 20.75) * mm, v(4.24, 20.67) * mm, v(4.33, 20.53) * mm, v(4.43, 20.47) * mm, v(4.55, 20.35) * mm, v(4.58, 20.31) * mm, v(4.68, 20.2) * mm, v(4.73, 20.1) * mm, v(4.86, 20.04) * mm, v(4.92, 19.94) * mm, v(5.04, 19.86) * mm, v(5.1, 19.82) * mm, v(5.22, 19.83) * mm, v(5.3, 19.68) * mm, v(5.34, 19.58) * mm, v(5.47, 19.54) * mm, v(5.6, 19.54) * mm, v(5.7, 19.56) * mm, v(5.78, 19.54) * mm, v(5.8, 19.5) * mm, v(5.87, 19.42) * mm, v(5.97, 19.32) * mm, v(6.05, 19.26) * mm, v(6.18, 19.2) * mm, v(6.22, 19.17) * mm, v(6.35, 19.1) * mm, v(6.4, 19.06) * mm, v(6.43, 19.02) * mm, v(6.52, 18.97) * mm, v(6.66, 18.88) * mm, v(6.73, 18.85) * mm, v(6.84, 18.82) * mm, v(6.98, 18.77) * mm, v(7.09, 18.72) * mm, v(7.2, 18.65) * mm, v(7.25, 18.62) * mm, v(7.39, 18.52) * mm, v(7.56, 18.42) * mm, v(7.58, 18.4) * mm, v(7.68, 18.35) * mm, v(7.76, 18.3) * mm, v(7.9, 18.23) * mm, v(7.96, 18.2) * mm, v(8.08, 18.1) * mm, v(8.11, 18.03) * mm, v(8.23, 17.98) * mm, v(8.3, 17.92) * mm, v(8.4, 17.85) * mm, v(8.51, 17.78) * mm, v(8.6, 17.7) * mm, v(8.67, 17.65) * mm, v(8.77, 17.56) * mm, v(8.86, 17.5) * mm, v(8.96, 17.42) * mm, v(9.06, 17.34) * mm, v(9.1, 17.3) * mm, v(9.22, 17.25) * mm, v(9.3, 17.18) * mm, v(9.4, 17.07) * mm, v(9.47, 17.07) * mm, v(9.59, 16.94) * mm, v(9.72, 16.87) * mm, v(9.78, 16.8) * mm, v(9.8, 16.74) * mm, v(9.9, 16.7) * mm, v(9.99, 16.66) * mm, v(10.07, 16.62) * mm, v(10.14, 16.58) * mm, v(10.2, 16.52) * mm, v(10.25, 16.46) * mm, v(10.3, 16.41) * mm, v(10.39, 16.38) * mm, v(10.5, 16.28) * mm, v(10.58, 16.23) * mm, v(10.66, 16.16) * mm, v(10.72, 16.09) * mm, v(10.85, 15.95) * mm, v(10.95, 15.88) * mm, v(11.02, 15.86) * mm, v(11.06, 15.85) * mm, v(11.08, 15.77) * mm, v(11.1, 15.7) * mm, v(11.13, 15.61) * mm, v(11.18, 15.57) * mm, v(11.26, 15.55) * mm, v(11.41, 15.5) * mm, v(11.42, 15.5) * mm, v(11.47, 15.44) * mm, v(11.5, 15.36) * mm, v(11.58, 15.26) * mm, v(11.72, 15.19) * mm, v(11.73, 15.2) * mm, v(11.84, 15.16) * mm, v(11.87, 15.11) * mm, v(11.94, 15.06) * mm, v(12.08, 14.96) * mm, v(12.08, 14.94) * mm, v(12.22, 14.87) * mm, v(12.3, 14.82) * mm, v(12.35, 14.69) * mm, v(12.4, 14.53) * mm, v(12.44, 14.44) * mm, v(12.54, 14.37) * mm, v(12.66, 14.33) * mm, v(12.74, 14.33) * mm, v(12.82, 14.31) * mm, v(12.94, 14.26) * mm, v(13.08, 14.19) * mm, v(13.2, 14.1) * mm, v(13.39, 13.96) * mm, v(13.51, 13.83) * mm], "startDerivative": vector(-30.43, 1.1) * mm, "endDerivative": vector(17.59, -21.1) * mm});
            skFitSpline(sketch, "E12", {"points": [v(13.51, 13.83) * mm, v(13.37, 13.83) * mm, v(13.23, 13.65) * mm, v(13.11, 13.6) * mm, v(13.04, 13.56) * mm, v(12.88, 13.49) * mm, v(12.82, 13.44) * mm, v(12.69, 13.36) * mm, v(12.54, 13.28) * mm, v(12.44, 13.19) * mm, v(12.34, 13.15) * mm, v(12.2, 13.1) * mm, v(12.09, 13.04) * mm, v(12.08, 12.97) * mm, v(11.9, 12.93) * mm, v(11.8, 12.89) * mm, v(11.73, 12.85) * mm, v(11.66, 12.8) * mm, v(11.5, 12.7) * mm, v(11.4, 12.63) * mm, v(11.28, 12.55) * mm, v(11.23, 12.52) * mm, v(11.12, 12.44) * mm, v(11, 12.37) * mm, v(10.87, 12.32) * mm, v(10.8, 12.27) * mm, v(10.69, 12.24) * mm, v(10.55, 12.18) * mm, v(10.49, 12.05) * mm, v(10.37, 12) * mm, v(10.18, 11.9) * mm, v(10.1, 11.84) * mm, v(10, 11.8) * mm, v(9.94, 11.77) * mm, v(9.83, 11.7) * mm, v(9.8, 11.67) * mm, v(9.75, 11.63) * mm, v(9.66, 11.6) * mm, v(9.6, 11.56) * mm, v(9.52, 11.48) * mm, v(9.45, 11.43) * mm], "startDerivative": vector(-5.65, 1.52) * mm, "endDerivative": vector(-3.52, -2.03) * mm});
            skFitSpline(sketch, "E13", {"points": [v(9.45, 11.43) * mm, v(9.32, 11.43) * mm, v(9.24, 11.43) * mm, v(9.2, 11.43) * mm, v(9.16, 11.43) * mm, v(9.09, 11.43) * mm, v(9.08, 11.43) * mm, v(9.03, 11.43) * mm, v(8.76, 11.48) * mm, v(8.68, 11.5) * mm, v(8.62, 11.52) * mm, v(8.5, 11.56) * mm, v(8.42, 11.57) * mm, v(7.14, 11.89) * mm, v(6.14, 12.1) * mm, v(5.6, 12.27) * mm, v(5.53, 12.2) * mm, v(5.32, 12.41) * mm, v(5.25, 12.5) * mm, v(5.22, 12.54) * mm, v(5.18, 12.73) * mm, v(5.08, 12.73) * mm, v(5.03, 12.68) * mm, v(4.98, 12.7) * mm, v(4.92, 12.67) * mm, v(4.85, 12.63) * mm, v(4.77, 12.6) * mm, v(4.63, 12.7) * mm, v(4.5, 12.73) * mm, v(4.42, 12.74) * mm, v(4.34, 12.74) * mm, v(4.25, 12.7) * mm, v(4.12, 12.76) * mm, v(4.03, 12.8) * mm, v(3.5, 12.9) * mm, v(3.21, 12.93) * mm, v(2.93, 13) * mm, v(2.58, 13.07) * mm, v(2.42, 13.08) * mm, v(2.32, 13.18) * mm, v(2.22, 13.34) * mm, v(2.07, 13.39) * mm, v(1.92, 13.3) * mm, v(1.8, 13.2) * mm, v(1.74, 13.3) * mm, v(1.6, 13.34) * mm, v(0.46, 13.39) * mm, v(-0.24, 13.54) * mm, v(-1.85, 13.9) * mm, v(-3.84, 14.55) * mm, v(-4.04, 14.6) * mm, v(-4.12, 14.84) * mm, v(-4.25, 14.88) * mm, v(-4.46, 14.84) * mm, v(-4.56, 14.92) * mm, v(-4.66, 14.88) * mm, v(-4.82, 15) * mm, v(-5, 15.09) * mm, v(-5.1, 15.09) * mm, v(-5.33, 15.13) * mm, v(-5.45, 15.21) * mm, v(-5.6, 15.17) * mm, v(-5.67, 15) * mm, v(-5.7, 14.86) * mm, v(-7.85, 15.46) * mm, v(-7.91, 15.65) * mm, v(-7.91, 15.86) * mm, v(-8.04, 16.05) * mm, v(-8.17, 16.12) * mm, v(-8.38, 16.09) * mm, v(-8.53, 15.94) * mm, v(-13.96, 17.33) * mm, v(-14.07, 17.49) * mm, v(-14.25, 17.49) * mm, v(-14.32, 17.43) * mm, v(-14.45, 17.3) * mm, v(-14.52, 17.25) * mm, v(-14.66, 17.38) * mm, v(-14.76, 17.45) * mm, v(-17.27, 17.77) * mm, v(-18.97, 18.35) * mm, v(-19, 18.58) * mm, v(-19.12, 18.63) * mm, v(-19.23, 18.66) * mm, v(-19.36, 18.71) * mm, v(-19.5, 18.8) * mm, v(-19.63, 18.8) * mm, v(-19.8, 18.8) * mm, v(-19.99, 18.8) * mm, v(-20.05, 18.8) * mm, v(-20.2, 18.86) * mm, v(-20.4, 19) * mm, v(-20.5, 18.9) * mm, v(-20.56, 18.79) * mm, v(-20.63, 18.65) * mm, v(-20.69, 18.55) * mm, v(-22.4, 19) * mm, v(-22.43, 19.05) * mm, v(-22.4, 19.2) * mm, v(-22.45, 19.33) * mm, v(-22.53, 19.54) * mm, v(-22.63, 19.66) * mm, v(-22.88, 19.78) * mm, v(-22.98, 19.7) * mm, v(-23.06, 19.66) * mm, v(-23.18, 19.6) * mm, v(-28.18, 20.83) * mm, v(-28.27, 20.96) * mm, v(-28.42, 21.04) * mm, v(-28.52, 21.05) * mm, v(-28.65, 21.07) * mm, v(-28.78, 20.97) * mm, v(-28.79, 20.94) * mm, v(-29.3, 20.97) * mm, v(-29.57, 20.98) * mm, v(-29.78, 20.99) * mm, v(-29.95, 20.99) * mm, v(-30.27, 21.04) * mm, v(-31.08, 21.2) * mm, v(-31.51, 21.32) * mm, v(-32.12, 21.52) * mm, v(-32.4, 21.72) * mm, v(-32.55, 21.82) * mm, v(-32.7, 21.85) * mm, v(-32.82, 21.9) * mm, v(-32.92, 21.97) * mm, v(-33.1, 21.94) * mm, v(-33.3, 22.04) * mm, v(-33.53, 22.16) * mm, v(-33.56, 22.3) * mm, v(-33.62, 22.43) * mm, v(-33.7, 22.58) * mm, v(-33.8, 22.63) * mm, v(-33.98, 22.62) * mm, v(-34.18, 22.56) * mm, v(-34.28, 22.5) * mm, v(-34.39, 22.47) * mm, v(-34.53, 22.46) * mm, v(-34.64, 22.45) * mm, v(-34.76, 22.62) * mm, v(-34.86, 22.73) * mm, v(-35.42, 22.97) * mm, v(-36.27, 23.35) * mm, v(-36.96, 23.66) * mm, v(-37.46, 23.86) * mm, v(-38.14, 24.12) * mm, v(-38.3, 24.24) * mm, v(-38.4, 24.5) * mm, v(-38.64, 24.67) * mm, v(-38.8, 24.72) * mm, v(-39, 24.74) * mm, v(-39.29, 24.67) * mm, v(-39.53, 24.47) * mm, v(-39.72, 24.24) * mm, v(-40, 23.9) * mm, v(-40.12, 23.4) * mm, v(-40.24, 23.07) * mm, v(-40.3, 22.64) * mm, v(-40.3, 22.28) * mm, v(-40.35, 21.7) * mm, v(-40.27, 21.29) * mm, v(-40.12, 20.95) * mm, v(-39.85, 20.6) * mm, v(-39.53, 20.51) * mm, v(-39.24, 20.58) * mm, v(-39.07, 20.74) * mm, v(-38.7, 20.74) * mm, v(-37.77, 20.66) * mm, v(-36.78, 20.6) * mm, v(-35.55, 20.57) * mm, v(-35.02, 20.55) * mm, v(-34.83, 20.17) * mm, v(-34.59, 20) * mm, v(-34.26, 20) * mm, v(-33.93, 20.25) * mm, v(-33.58, 20.25) * mm, v(-33.23, 20.2) * mm, v(-32.96, 20.17) * mm, v(-32.6, 20.22) * mm, v(-32.3, 20.27) * mm, v(-31.96, 20.17) * mm, v(-31.6, 20.08) * mm, v(-31.3, 19.98) * mm, v(-30.95, 19.9) * mm, v(-30.7, 19.81) * mm, v(-30.06, 19.6) * mm, v(-29.68, 19.43) * mm, v(-29.46, 19.24) * mm, v(-29.22, 19.14) * mm, v(-29.1, 18.97) * mm, v(-28.76, 18.97) * mm, v(-28.43, 18.86) * mm, v(-28.16, 18.92) * mm, v(-27.7, 18.81) * mm, v(-27.21, 18.67) * mm, v(-27, 18.67) * mm, v(-26.29, 18.51) * mm, v(-26.04, 18.48) * mm, v(-25.15, 18.3) * mm, v(-24.74, 18.1) * mm, v(-24.17, 18.02) * mm, v(-23.98, 17.97) * mm, v(-23.5, 17.78) * mm, v(-23.36, 17.56) * mm, v(-23.21, 17.56) * mm, v(-23.03, 17.54) * mm, v(-22.86, 17.63) * mm, v(-22.81, 17.67) * mm, v(-22.75, 17.73) * mm, v(-22.67, 17.83) * mm, v(-22.61, 17.95) * mm, v(-22.08, 17.87) * mm, v(-21.6, 17.75) * mm, v(-21.3, 17.63) * mm, v(-20.97, 17.6) * mm, v(-20.96, 17.49) * mm, v(-20.96, 17.3) * mm, v(-20.92, 17.18) * mm, v(-20.82, 17.07) * mm, v(-20.61, 17.07) * mm, v(-20.49, 17.07) * mm, v(-20.37, 17.07) * mm, v(-20.2, 17.07) * mm, v(-20.03, 16.94) * mm, v(-19.88, 16.88) * mm, v(-19.62, 16.78) * mm, v(-19.55, 16.78) * mm, v(-19.3, 16.83) * mm, v(-19.24, 16.83) * mm, v(-19.2, 16.94) * mm, v(-18.62, 16.83) * mm, v(-18.49, 16.81) * mm, v(-18.27, 16.78) * mm, v(-18.02, 16.75) * mm, v(-17.88, 16.7) * mm, v(-17.73, 16.7) * mm, v(-17.52, 16.63) * mm, v(-17.35, 16.58) * mm, v(-17.2, 16.54) * mm, v(-17.06, 16.5) * mm, v(-16.88, 16.47) * mm, v(-16.78, 16.44) * mm, v(-16.7, 16.4) * mm, v(-16.57, 16.37) * mm, v(-16.4, 16.3) * mm, v(-16.24, 16.27) * mm, v(-16.08, 16.22) * mm, v(-15.97, 16.16) * mm, v(-15.84, 16.1) * mm, v(-15.72, 16.06) * mm, v(-15.53, 15.98) * mm, v(-15.38, 15.92) * mm, v(-15.28, 15.88) * mm, v(-15.14, 15.83) * mm, v(-15.1, 15.74) * mm, v(-14.95, 15.73) * mm, v(-14.84, 15.8) * mm, v(-14.75, 15.53) * mm, v(-14.6, 15.46) * mm, v(-14.48, 15.47) * mm, v(-14.41, 15.55) * mm, v(-14.24, 15.57) * mm, v(-14.1, 15.51) * mm, v(-14.03, 15.47) * mm, v(-13.93, 15.44) * mm, v(-13.72, 15.44) * mm, v(-13.61, 15.42) * mm, v(-13.49, 15.4) * mm, v(-13.27, 15.39) * mm, v(-13.14, 15.38) * mm, v(-13.04, 15.35) * mm, v(-12.88, 15.3) * mm, v(-12.55, 15.21) * mm, v(-12.17, 15.15) * mm, v(-12.07, 15.15) * mm, v(-11.9, 15.14) * mm, v(-11.78, 15.11) * mm, v(-11.62, 15.07) * mm, v(-11.5, 15.03) * mm, v(-11.31, 14.98) * mm, v(-11.17, 14.94) * mm, v(-11.04, 14.9) * mm, v(-10.89, 14.85) * mm, v(-10.66, 14.8) * mm, v(-10.6, 14.8) * mm, v(-10.47, 14.76) * mm, v(-10.35, 14.73) * mm, v(-9.83, 14.53) * mm, v(-9.54, 14.48) * mm, v(-9.25, 14.4) * mm, v(-8.9, 14.28) * mm, v(-8.88, 14.11) * mm, v(-8.83, 13.98) * mm, v(-8.7, 13.83) * mm, v(-8.51, 13.83) * mm, v(-8.28, 14) * mm, v(-8.17, 14.16) * mm, v(-8.13, 14.3) * mm, v(-8.04, 14.35) * mm, v(-7.82, 14.26) * mm, v(-7.63, 14.25) * mm, v(-7.45, 14.21) * mm, v(-7.22, 14.15) * mm, v(-7.12, 14.12) * mm, v(-6.98, 14.07) * mm, v(-6.76, 13.98) * mm, v(-6.5, 13.93) * mm, v(-6.34, 13.83) * mm, v(-6.13, 13.83) * mm, v(-6.02, 13.83) * mm, v(-6.09, 13.52) * mm, v(-6.03, 13.35) * mm, v(-5.74, 13.3) * mm, v(-5.48, 13.32) * mm, v(-5.38, 13.32) * mm, v(-5.2, 13.26) * mm, v(-5.13, 13.14) * mm, v(-4.95, 13.09) * mm, v(-4.85, 13.09) * mm, v(-4.7, 13.17) * mm, v(-4.6, 13.2) * mm, v(-4.49, 13.22) * mm, v(-4.27, 13.22) * mm, v(-4.06, 13.19) * mm, v(-3.96, 13.14) * mm, v(-3.73, 13.08) * mm, v(-3.5, 13.05) * mm, v(-3.27, 13) * mm, v(-3.09, 12.96) * mm, v(-3, 12.95) * mm, v(-2.78, 12.92) * mm, v(-2.64, 12.88) * mm, v(-2.47, 12.83) * mm, v(-2.4, 12.8) * mm, v(-1.95, 12.67) * mm, v(-1.7, 12.62) * mm, v(-1.42, 12.54) * mm, v(-1.12, 12.49) * mm, v(-0.9, 12.4) * mm, v(-0.5, 12.32) * mm, v(-0.33, 12.26) * mm, v(0, 12.14) * mm, v(0.28, 12.08) * mm, v(0.47, 12) * mm, v(0.71, 11.89) * mm, v(0.78, 11.79) * mm, v(1.04, 11.68) * mm, v(1.16, 11.61) * mm, v(1.2, 11.43) * mm, v(1.38, 11.43) * mm, v(1.48, 11.3) * mm, v(1.62, 11.19) * mm, v(1.8, 11.22) * mm, v(1.94, 11.3) * mm, v(2.13, 11.3) * mm, v(2.42, 11.15) * mm, v(3.03, 11.05) * mm, v(3.27, 10.93) * mm, v(3.63, 10.73) * mm, v(3.74, 10.68) * mm, v(4.11, 10.6) * mm, v(4.18, 10.57) * mm, v(4.37, 10.4) * mm, v(4.47, 10.28) * mm, v(4.62, 10.35) * mm, v(4.73, 10.53) * mm, v(5.02, 10.46) * mm, v(5.24, 10.4) * mm, v(5.47, 10.37) * mm, v(5.71, 10.26) * mm, v(5.95, 10.24) * mm, v(6.18, 10.19) * mm, v(6.44, 10.15) * mm, v(6.62, 10.14) * mm, v(6.78, 10.03) * mm, v(6.94, 9.97) * mm], "startDerivative": vector(-67.79, 0) * mm, "endDerivative": vector(73.6, -15.9) * mm});
            skFitSpline(sketch, "E14", {"points": [v(6.94, 9.97) * mm, v(6.8, 9.8) * mm, v(6.64, 9.67) * mm, v(6.34, 9.48) * mm, v(6.18, 9.35) * mm, v(5.89, 9.2) * mm, v(5.68, 9.02) * mm, v(5.26, 8.74) * mm, v(4.98, 8.56) * mm, v(4.7, 8.35) * mm, v(4.52, 8.23) * mm, v(4.3, 8.12) * mm, v(3.98, 7.81) * mm, v(3.75, 7.7) * mm, v(3.55, 7.55) * mm, v(3.24, 7.2) * mm, v(3.1, 7.22) * mm, v(2.86, 7.03) * mm, v(2.63, 6.82) * mm, v(2.36, 6.64) * mm, v(2.13, 6.49) * mm, v(1.96, 6.26) * mm, v(1.73, 6.09) * mm, v(1.48, 5.95) * mm, v(1.12, 5.65) * mm, v(0.85, 5.43) * mm, v(0.6, 5.26) * mm, v(0.4, 5.03) * mm, v(0, 4.92) * mm, v(-0.59, 4.28) * mm, v(-0.8, 4.15) * mm, v(-1.07, 3.94) * mm, v(-1.36, 3.73) * mm, v(-1.5, 3.56) * mm, v(-1.72, 3.29) * mm, v(-2.05, 3.1) * mm, v(-2.18, 2.9) * mm, v(-2.43, 2.64) * mm, v(-2.54, 2.39) * mm, v(-2.89, 2.18) * mm, v(-3.04, 2) * mm, v(-3.18, 1.83) * mm, v(-3.27, 1.62) * mm, v(-3.43, 1.45) * mm, v(-3.6, 1.27) * mm, v(-3.81, 1.08) * mm, v(-3.96, 0.74) * mm, v(-4.23, 0.53) * mm, v(-4.23, 0) * mm, v(-4.4, 0) * mm, v(-4.4, -0.3) * mm, v(-4.4, -0.7) * mm, v(-4.4, -0.94) * mm, v(-4.4, -1.17) * mm, v(-4.6, -1.34) * mm, v(-4.65, -1.61) * mm, v(-4.73, -1.77) * mm, v(-4.75, -2.15) * mm, v(-4.73, -2.4) * mm, v(-4.71, -2.72) * mm, v(-4.71, -3.01) * mm, v(-4.77, -3.34) * mm, v(-4.61, -3.6) * mm, v(-4.4, -3.84) * mm, v(-4.4, -4) * mm], "startDerivative": vector(-11.31, -13.99) * mm, "endDerivative": vector(-3.02, -14.68) * mm});
            skLineSegment(sketch, "E15", {"start": v(9.45, 11.43) * mm, "end": v(9.47, 11.36) * mm});
            skLineSegment(sketch, "E16", {"start": v(9.47, 11.36) * mm, "end": v(9.52, 11.35) * mm});
            skLineSegment(sketch, "E17", {"start": v(9.52, 11.35) * mm, "end": v(9.55, 11.35) * mm});
            skLineSegment(sketch, "E18", {"start": v(9.55, 11.35) * mm, "end": v(9.59, 11.34) * mm});
            skLineSegment(sketch, "E19", {"start": v(9.59, 11.34) * mm, "end": v(9.68, 11.32) * mm});
            skLineSegment(sketch, "E20", {"start": v(9.68, 11.32) * mm, "end": v(9.76, 11.33) * mm});
            skLineSegment(sketch, "E21", {"start": v(9.76, 11.33) * mm, "end": v(9.85, 11.3) * mm});
            skLineSegment(sketch, "E22", {"start": v(9.85, 11.3) * mm, "end": v(10, 11.27) * mm});
            skLineSegment(sketch, "E23", {"start": v(10, 11.27) * mm, "end": v(10.04, 11.25) * mm});
            skLineSegment(sketch, "E24", {"start": v(10.04, 11.25) * mm, "end": v(10.1, 11.24) * mm});
            skLineSegment(sketch, "E25", {"start": v(10.1, 11.24) * mm, "end": v(10.17, 11.23) * mm});
            skLineSegment(sketch, "E26", {"start": v(10.17, 11.23) * mm, "end": v(10.24, 11.22) * mm});
            skLineSegment(sketch, "E27", {"start": v(10.24, 11.22) * mm, "end": v(10.3, 11.21) * mm});
            skLineSegment(sketch, "E28", {"start": v(10.3, 11.21) * mm, "end": v(10.37, 11.2) * mm});
            skLineSegment(sketch, "E29", {"start": v(10.37, 11.2) * mm, "end": v(10.44, 11.18) * mm});
            skLineSegment(sketch, "E30", {"start": v(10.44, 11.18) * mm, "end": v(10.5, 11.19) * mm});
            skLineSegment(sketch, "E31", {"start": v(10.5, 11.19) * mm, "end": v(10.56, 11.19) * mm});
            skLineSegment(sketch, "E32", {"start": v(10.56, 11.19) * mm, "end": v(10.63, 11.16) * mm});
            skLineSegment(sketch, "E33", {"start": v(10.63, 11.16) * mm, "end": v(10.68, 11.15) * mm});
            skLineSegment(sketch, "E34", {"start": v(10.68, 11.15) * mm, "end": v(10.76, 11.13) * mm});
            skLineSegment(sketch, "E35", {"start": v(10.76, 11.13) * mm, "end": v(10.83, 11.1) * mm});
            skLineSegment(sketch, "E36", {"start": v(10.83, 11.1) * mm, "end": v(11.25, 11.02) * mm});
            skLineSegment(sketch, "E37", {"start": v(11.25, 11.02) * mm, "end": v(11.34, 10.99) * mm});
            skLineSegment(sketch, "E38", {"start": v(11.34, 10.99) * mm, "end": v(11.43, 10.98) * mm});
            skLineSegment(sketch, "E39", {"start": v(11.43, 10.98) * mm, "end": v(11.46, 10.95) * mm});
            skLineSegment(sketch, "E40", {"start": v(11.46, 10.95) * mm, "end": v(11.57, 10.95) * mm});
            skLineSegment(sketch, "E41", {"start": v(11.57, 10.95) * mm, "end": v(11.7, 10.93) * mm});
            skLineSegment(sketch, "E42", {"start": v(11.7, 10.93) * mm, "end": v(11.8, 10.9) * mm});
            skLineSegment(sketch, "E43", {"start": v(11.8, 10.9) * mm, "end": v(11.93, 10.88) * mm});
            skLineSegment(sketch, "E44", {"start": v(11.93, 10.88) * mm, "end": v(12.1, 10.87) * mm});
            skLineSegment(sketch, "E45", {"start": v(12.1, 10.87) * mm, "end": v(12.3, 10.8) * mm});
            skLineSegment(sketch, "E46", {"start": v(12.3, 10.8) * mm, "end": v(12.37, 10.78) * mm});
            skLineSegment(sketch, "E47", {"start": v(12.37, 10.78) * mm, "end": v(12.47, 10.75) * mm});
            skLineSegment(sketch, "E48", {"start": v(12.47, 10.75) * mm, "end": v(12.6, 10.69) * mm});
            skLineSegment(sketch, "E49", {"start": v(12.6, 10.69) * mm, "end": v(12.75, 10.63) * mm});
            skLineSegment(sketch, "E50", {"start": v(12.75, 10.63) * mm, "end": v(12.82, 10.62) * mm});
            skLineSegment(sketch, "E51", {"start": v(12.82, 10.62) * mm, "end": v(12.98, 10.58) * mm});
            skLineSegment(sketch, "E52", {"start": v(12.98, 10.58) * mm, "end": v(13.06, 10.53) * mm});
            skLineSegment(sketch, "E53", {"start": v(13.06, 10.53) * mm, "end": v(13.3, 10.44) * mm});
            skLineSegment(sketch, "E54", {"start": v(13.3, 10.44) * mm, "end": v(13.38, 10.4) * mm});
            skLineSegment(sketch, "E55", {"start": v(13.38, 10.4) * mm, "end": v(13.58, 10.35) * mm});
            skLineSegment(sketch, "E56", {"start": v(13.58, 10.35) * mm, "end": v(13.83, 10.34) * mm});
            skLineSegment(sketch, "E57", {"start": v(13.83, 10.34) * mm, "end": v(13.98, 10.34) * mm});
            skLineSegment(sketch, "E58", {"start": v(13.98, 10.34) * mm, "end": v(14.28, 10.35) * mm});
            skLineSegment(sketch, "E59", {"start": v(14.28, 10.35) * mm, "end": v(14.36, 10.3) * mm});
            skLineSegment(sketch, "E60", {"start": v(14.36, 10.3) * mm, "end": v(14.36, 10.18) * mm});
            skLineSegment(sketch, "E61", {"start": v(14.36, 10.18) * mm, "end": v(14.36, 9.91) * mm});
            skLineSegment(sketch, "E62", {"start": v(14.36, 9.91) * mm, "end": v(14.22, 9.54) * mm});
            skLineSegment(sketch, "E63", {"start": v(14.22, 9.54) * mm, "end": v(14.24, 9.36) * mm});
            skLineSegment(sketch, "E64", {"start": v(14.24, 9.36) * mm, "end": v(14.2, 9.25) * mm});
            skLineSegment(sketch, "E65", {"start": v(14.2, 9.25) * mm, "end": v(14.2, 9.18) * mm});
            skLineSegment(sketch, "E66", {"start": v(14.2, 9.18) * mm, "end": v(14.17, 9.1) * mm});
            skLineSegment(sketch, "E67", {"start": v(14.17, 9.1) * mm, "end": v(14.17, 9.01) * mm});
            skLineSegment(sketch, "E68", {"start": v(14.17, 9.01) * mm, "end": v(14.12, 8.94) * mm});
            skLineSegment(sketch, "E69", {"start": v(14.12, 8.94) * mm, "end": v(14.09, 8.88) * mm});
            skLineSegment(sketch, "E70", {"start": v(14.09, 8.88) * mm, "end": v(14.05, 8.82) * mm});
            skLineSegment(sketch, "E71", {"start": v(14.05, 8.82) * mm, "end": v(14.04, 8.74) * mm});
            skLineSegment(sketch, "E72", {"start": v(14.04, 8.74) * mm, "end": v(14.02, 8.64) * mm});
            skLineSegment(sketch, "E73", {"start": v(14.02, 8.64) * mm, "end": v(13.91, 8.37) * mm});
            skLineSegment(sketch, "E74", {"start": v(13.91, 8.37) * mm, "end": v(13.8, 8.2) * mm});
            skLineSegment(sketch, "E75", {"start": v(13.8, 8.2) * mm, "end": v(13.77, 8.15) * mm});
            skLineSegment(sketch, "E76", {"start": v(13.77, 8.15) * mm, "end": v(13.72, 8.1) * mm});
            skLineSegment(sketch, "E77", {"start": v(13.72, 8.1) * mm, "end": v(13.55, 7.97) * mm});
            skLineSegment(sketch, "E78", {"start": v(13.55, 7.97) * mm, "end": v(13.5, 7.9) * mm});
            skLineSegment(sketch, "E79", {"start": v(13.5, 7.9) * mm, "end": v(13.4, 7.88) * mm});
            skLineSegment(sketch, "E80", {"start": v(13.4, 7.88) * mm, "end": v(13.34, 7.94) * mm});
            skLineSegment(sketch, "E81", {"start": v(13.34, 7.94) * mm, "end": v(13.34, 8.09) * mm});
            skLineSegment(sketch, "E82", {"start": v(13.34, 8.09) * mm, "end": v(13.37, 8.17) * mm});
            skLineSegment(sketch, "E83", {"start": v(13.37, 8.17) * mm, "end": v(13.41, 8.25) * mm});
            skLineSegment(sketch, "E84", {"start": v(13.41, 8.25) * mm, "end": v(13.47, 8.36) * mm});
            skLineSegment(sketch, "E85", {"start": v(13.47, 8.36) * mm, "end": v(13.52, 8.47) * mm});
            skLineSegment(sketch, "E86", {"start": v(13.52, 8.47) * mm, "end": v(13.54, 8.6) * mm});
            skLineSegment(sketch, "E87", {"start": v(13.54, 8.6) * mm, "end": v(13.53, 8.67) * mm});
            skLineSegment(sketch, "E88", {"start": v(13.53, 8.67) * mm, "end": v(13.54, 8.77) * mm});
            skLineSegment(sketch, "E89", {"start": v(13.54, 8.77) * mm, "end": v(13.55, 8.85) * mm});
            skLineSegment(sketch, "E90", {"start": v(13.55, 8.85) * mm, "end": v(13.57, 8.96) * mm});
            skLineSegment(sketch, "E91", {"start": v(13.57, 8.96) * mm, "end": v(13.58, 9.07) * mm});
            skLineSegment(sketch, "E92", {"start": v(13.58, 9.07) * mm, "end": v(13.6, 9.1) * mm});
            skLineSegment(sketch, "E93", {"start": v(13.6, 9.1) * mm, "end": v(13.63, 9.2) * mm});
            skLineSegment(sketch, "E94", {"start": v(13.63, 9.2) * mm, "end": v(13.67, 9.28) * mm});
            skLineSegment(sketch, "E95", {"start": v(13.67, 9.28) * mm, "end": v(13.72, 9.37) * mm});
            skLineSegment(sketch, "E96", {"start": v(13.72, 9.37) * mm, "end": v(13.78, 9.44) * mm});
            skLineSegment(sketch, "E97", {"start": v(13.78, 9.44) * mm, "end": v(13.82, 9.53) * mm});
            skLineSegment(sketch, "E98", {"start": v(13.82, 9.53) * mm, "end": v(13.8, 9.64) * mm});
            skLineSegment(sketch, "E99", {"start": v(13.8, 9.64) * mm, "end": v(13.78, 9.74) * mm});
            skLineSegment(sketch, "E100", {"start": v(13.78, 9.74) * mm, "end": v(13.9, 9.94) * mm});
            skLineSegment(sketch, "E101", {"start": v(13.9, 9.94) * mm, "end": v(13.92, 10.02) * mm});
            skLineSegment(sketch, "E102", {"start": v(13.92, 10.02) * mm, "end": v(13.9, 10.1) * mm});
            skLineSegment(sketch, "E103", {"start": v(13.9, 10.1) * mm, "end": v(13.9, 10.18) * mm});
            skLineSegment(sketch, "E104", {"start": v(13.9, 10.18) * mm, "end": v(13.87, 10.25) * mm});
            skLineSegment(sketch, "E105", {"start": v(13.87, 10.25) * mm, "end": v(13.85, 10.3) * mm});
            skFitSpline(sketch, "E106", {"points": [v(13.85, 10.3) * mm, v(13.83, 10.34) * mm], "startDerivative": vector(-0.02, 0.05) * mm, "endDerivative": vector(-0.02, 0.05) * mm});
            skSolve(sketch);
        }
        {
            var Q0;
            Q0 = qSketchRegion(id + "F0", true);
            extrude(context, id + "F1", {"entities" : qUnion([Q0]), "depth" : 2 * mm});
        }
    });
